# Revit family: IS_Idealrain_BD142_BIM_NL
name_source: partatom
category: Plumbing Fixtures
units: mm (PartAtom-declared; Revit-internal decimal feet)

## family parameters
Always vertical = No
Cut with Voids When Loaded = No
OmniClass Number = 23.45.05.14.17
OmniClass Title = Showers
Part Type = Normal
Room Calculation Point = No
Round Connector Dimension = Use Diameter
Shared = No
Work Plane-Based = No

## types (1)
- BD142XG - IDEALRAIN M1 SHOWER KIT 1F/100 600MM IF/175 - SILK BLACK
    Accesoires = https://www.idealstandard.nl
    Accessories = https://www.idealstandard.nl
    Afmetingen = 148 x 185 x 619 mm
    AfstandsEenheid = Millimeter
    Afwerking = Seide schwarz
    AreaUnits = Millimetres
    Artikelnummer = BD142XG
    Artikelomschrijving = IDEALRAIN M1 DUSCHE KIT 1F/100 600MM IF/175
    Artikelreferentie = IDEALRAIN M1 SHOWER KIT 1F/100 600MM IF/175
    Auteur = Ideal Standard
    BIMObjectName = IS_IdealStandard_Showermixers_Idealrain_BD142
    BIMobject category = Sanitary
    BIMobject category code = Taps & Mixers
    BIMobject main category = Sanitary
    BarCode = 3800861101208
    Barcode = 3800861101208
    Bedieningkraan = Handbuch
    Bedieningkraanwerk = drehen wissen
    Beschrijvinggarantie = Herstellergarantie
    BimObjectNaam = IS_IdealStandard_Showermixers_Idealrain_BD142
    Brand = Ideal Standard
    Brand url = http://www.idealstandard.nl
    Breedte = 147.669792
    BrutoGewicht = 0
    Color = Seide schwarz
    ConnectionType = Installation
    Cost = 0 $
    CurrencyUnit = €
    CurrentRevision = 1
    Date of publishing = 24/07/2021
    Description = IDEALRAIN M1 DUSCHE KIT 1F/100 600MM IF/175 - SEIDE SCHWARZ
    Diepte = 185 mm
    Douchebak = No
    DurationUnit = Years
    Edition number = 1
    Eigenschappen = M1 DUSCHE KIT 1F/100 600MM IF/175 - SEIDE SCHWARZ
    Features = M1 DUSCHE KIT 1F/100 600MM IF/175 - SEIDE SCHWARZ
    Finish = Seide schwarz
    GTIN code = https://3800861101208
    Garantieonderdelen = 5
    Garantieunits = Jaren
    GemaaktOp = 27/07/2021
    HasIntegralShutOffDevice = No
    Help = https://www.idealstandard.nl
    Hoogte = 619
    Hulp = https://www.idealstandard.nl
    IFC Classification = Sanitary Terminal
    IfcExportAs = IfcValveType
    IfcExportType = MIXING
    Installatieinstructies = https://www.idealstandard.nl
    Installation instructions = https://www.idealstandard.nl
    InstallationInstructions = https://www.idealstandard.nl
    IsBuiltIn = No
    IsHighPressure = No
    Kleur = Seide schwarz
    Lengte = 0 mm  [stored 0 ft]
    LinearUnits = Millimetres
    MainColor = Seide schwarz
    MaintenanceInformation = https://www.idealstandard.nl
    Manufacturer = Ideal Standard
    Manufacturer name = Ideal Standard
    ManufacturerURL = https://www.idealstandard.nl
    Materiaal = Messing
    Material = Brass
    Material main = Brass
    Merk = Ideal Standard
    Model = BD142XG
    ModelNumber = BD142XG
    ModelReference = IDEALRAIN M1 SHOWER KIT 1F/100 600MM IF/175
    Montageinstuctie = https://www.idealstandard.nl
    NBS Reference Code = 45-35-70/335
    NBS Reference Description = Shower mixers
    Name = Showermixers_Idealrain_BD142_IdealStandard
    NettWeight = 1.24
    Nettogewicht = 1.24
    NominalDepth = 185 mm
    NominalHeight = 619 mm
    NominalLength = 185 mm
    NominalWidth = 148 mm
    Normen = Showermixers_Idealrain_BD142_IdealStandard
    OppervlakteEenheid = Millimeter
    Product Guid = cd31aae1-5fbc-49ce-9cb7-9e3a966fbd51
    Product SKU = BD142
    Product certification = https://www.idealstandard.nl
    Product data url = https://bimobject.com
    Product family = Sanitary
    Product group = Showers
    Product name = IDEALRAIN M1 SHOWER KIT 1F/100 600MM IF/175
    Product url = https://www.idealstandard.nl
    ProductInformation = https://www.idealstandard.nl
    ProductSoort = Sanitary
    Productinformatie = https://www.idealstandard.nl
    QR code = http://bimobject.com
    Referentie = IDEALRAIN M1 SHOWER KIT 1F/100 600MM IF/175
    Revisie = 1
    Shape = Cylindrical
    Size = 148 x 185 x 619 mm
    Space = Internal
    SpareParts = https://www.idealstandard.nl
    Technical description = https://www.idealstandard.nl
    Telefoonnummer = 077 355 08 08
    TestPressure = 10 Bar
    Testdruk = 10 Bar
    Typeconnectie = Installation
    URL = https://www.idealstandard.nl
    Uniclass 2015 Code = Pr_40_20_87_80
    Uniclass 2015 Name = Shower thermostatic valves
    Uniclass2015Beschrijving = Shower thermostatic valves
    Uniclass2015Code = Pr_40_20_87_80
    Uniclass2015Referentie = Pr_40_20_87_80
    Uniclass2015Title = Shower thermostatic valves
    Uniclass2015Version = v1.22
    Urlproducent = https://www.idealstandard.nl
    ValutaEenheid = Euro
    Versie = 1
    Version = 1
    Vervangingskosten = 0
    VolumeUnits = Litres
    Volumeunits = Liters
    Vorm = zylindrisch
    WRASURL = https://www.wrasapprovals.co.uk
    WarrantyDescription = Manufacturer warranty
    WarrantyDurationUnit = Years
    Wisselstukken = https://www.idealstandard.nl
    Youtube clip = https://www.youtube.com

note: [stored X ft] marks values corroborated as IEEE doubles in the binary element streams (Revit-internal decimal feet)

## geometry (parser evidence)
native form markers: Sweep x3
no freeform markers — native parametric forms only
